# Revit family: Cim733_776
name_source: partatom
category: Pipe Accessories
revit_build: Autodesk Revit 2016 (Build: 20150220_1215(x64)
units: mm (PartAtom-declared; Revit-internal decimal feet)

## family parameters
Always vertical = Yes
Cut with Voids When Loaded = No
OmniClass Number = 23.75.00.00
OmniClass Title = Climate Control (HVAC)
Part Type = Normal
Round Connector Dimension = Use Diameter
Shared = No
Work Plane-Based = No

## types (3) — shared parameters
A = 80 mm
Black plastic = Black plastic
Blue plastic = Blue plastic
Brass = Brass
Operating temperature = -10 ÷ 120 °C
PN = 25
Red plastic = Red plastic
White plastic = White plastic
g = 10 mm  [stored 0.0328084 ft]
r2 = 14 mm  [stored 0.0459318 ft]
s = 22 mm  [stored 0.0721785 ft]
v = 18 mm  [stored 0.0590551 ft]

## per-type parameters (varying)
- 1/2''x1/2": 2d=15 mm  [stored 0.0492126 ft]; B=80 mm; B1=29 mm  [stored 0.0951444 ft]; B2=28 mm  [stored 0.0918635 ft]; C=42 mm; CH=16 mm; CH/2-1=15 mm  [stored 0.0492126 ft]; Chromed metal=Metallo cromato; D=14 mm  [stored 0.0459318 ft]; D1=15 mm  [stored 0.0492126 ft]; D2=30 mm  [stored 0.0984252 ft]; D3=19 mm  [stored 0.062336 ft]; D4=36 mm  [stored 0.11811 ft]; D5=8 mm  [stored 0.0262467 ft]; DN=10 mm  [stored 0.0328084 ft]; E=100 mm; E-50=50 mm  [stored 0.164042 ft]; Light blue plastic=Light blue plastic; d=8 mm  [stored 0.0262467 ft]; dist=126 mm; dist1=52 mm; dist2=33 mm  [stored 0.108268 ft]; distm=100 mm; dn=9 mm  [stored 0.0295276 ft]; dss=29 mm  [stored 0.0951444 ft]; dss2=72 mm  [stored 0.23622 ft]; dss3=113 mm; f1=63 mm; f2=17 mm; r=12 mm  [stored 0.0393701 ft]; r1=12 mm  [stored 0.0393701 ft]; r4=12 mm  [stored 0.0393701 ft]; rr=11 mm  [stored 0.0360892 ft]
- 3/4"x3/4": 2d=20 mm  [stored 0.0656168 ft]; B=82 mm; B1=33 mm  [stored 0.108268 ft]; B2=31 mm  [stored 0.101706 ft]; C=61 mm; CH=19 mm  [stored 0.062336 ft]; CH/2-1=18 mm  [stored 0.0590551 ft]; Chromed metal=Chromed metal; D=15 mm  [stored 0.0492126 ft]; D1=19 mm  [stored 0.062336 ft]; D2=27 mm  [stored 0.0885827 ft]; D3=20 mm  [stored 0.0656168 ft]; D4=36 mm  [stored 0.11811 ft]; D5=6 mm  [stored 0.019685 ft]; DN=12 mm  [stored 0.0393701 ft]; E=100 mm; E-50=50 mm  [stored 0.164042 ft]; Light blue plastic=Light blue plastic; d=10 mm  [stored 0.0328084 ft]; dist=133 mm; dist1=55 mm  [stored 0.180446 ft]; dist2=36 mm  [stored 0.11811 ft]; distm=106 mm; dn=11 mm  [stored 0.0360892 ft]; dss=38 mm; dss2=79 mm; dss3=119 mm; f1=65 mm; f2=19 mm  [stored 0.062336 ft]; r=15 mm  [stored 0.0492126 ft]; r1=14 mm  [stored 0.0459318 ft]; r4=15 mm  [stored 0.0492126 ft]; rr=14 mm  [stored 0.0459318 ft]
- 1"x1": 2d=25 mm  [stored 0.082021 ft]; B=91 mm; B1=35 mm; B2=41 mm; C=78 mm; CH=24 mm  [stored 0.0787402 ft]; CH/2-1=23 mm  [stored 0.0754593 ft]; Chromed metal=<By Category>; D=21 mm  [stored 0.0688976 ft]; D1=0 mm  [stored 0 ft]; D2=35 mm; D3=18 mm  [stored 0.0590551 ft]; D4=15 mm  [stored 0.0492126 ft]; D5=6 mm  [stored 0.019685 ft]; DN=16 mm; E=150 mm; E-50=100 mm; Light blue plastic=<By Category>; d=13 mm; dist=153 mm; dist1=65 mm; dist2=46 mm  [stored 0.150919 ft]; distm=128 mm; dn=15 mm  [stored 0.0492126 ft]; dss=47 mm; dss2=95 mm; dss3=140 mm; f1=74 mm; f2=23 mm  [stored 0.0754593 ft]; r=19 mm  [stored 0.062336 ft]; r1=14 mm  [stored 0.0459318 ft]; r4=19 mm  [stored 0.062336 ft]; rr=18 mm  [stored 0.0590551 ft]

note: [stored X ft] marks values corroborated as IEEE doubles in the binary element streams (Revit-internal decimal feet)

## geometry (parser evidence)
native form markers: Sweep x21
no freeform markers — native parametric forms only
